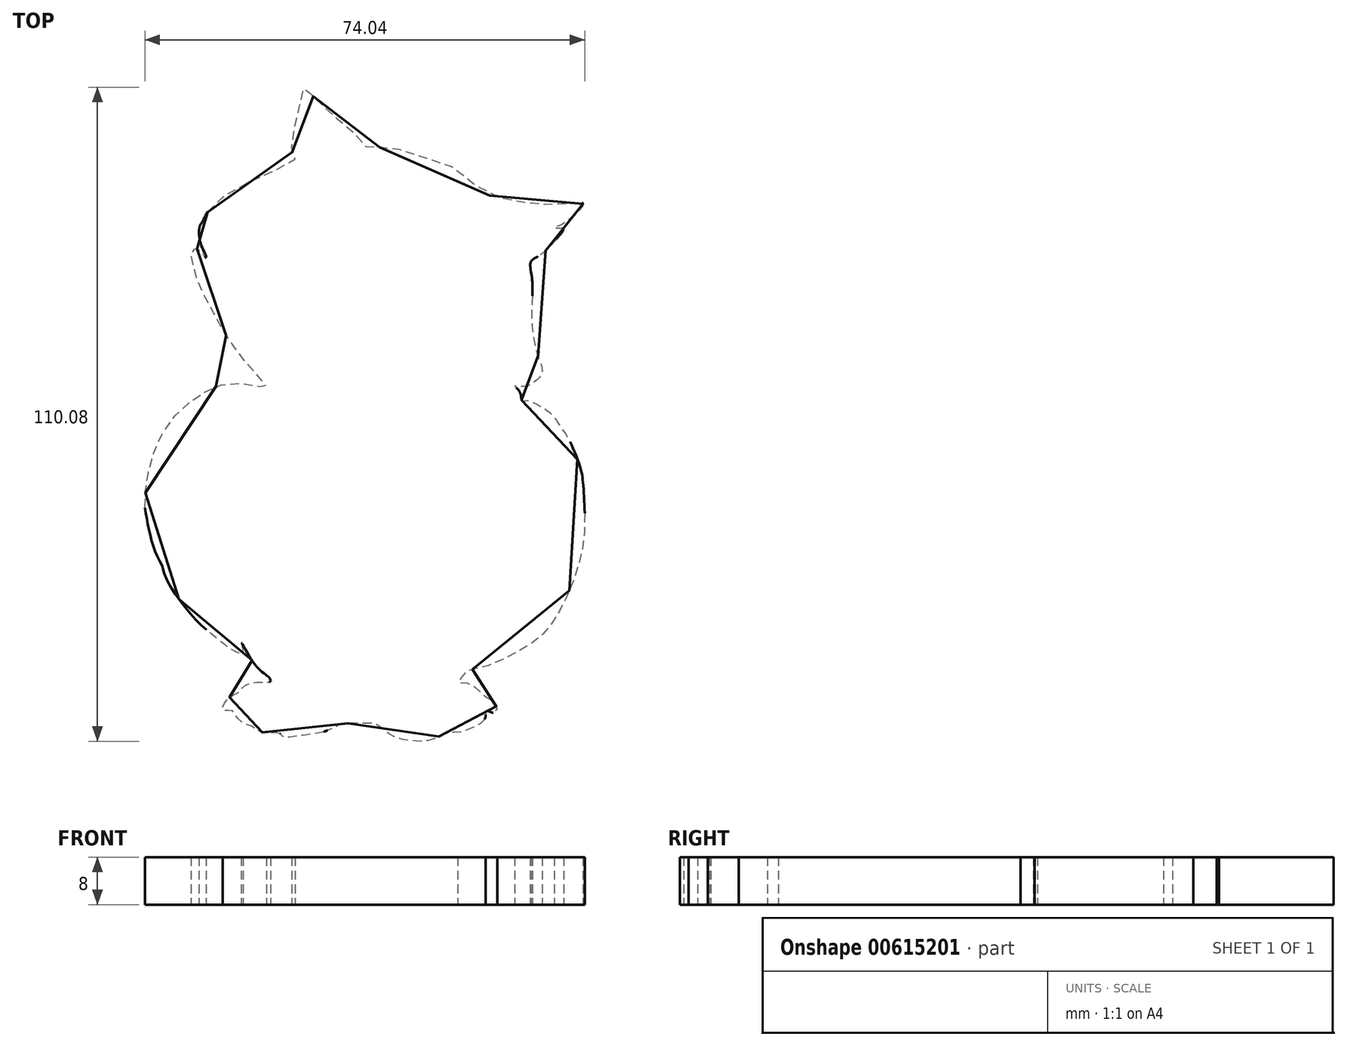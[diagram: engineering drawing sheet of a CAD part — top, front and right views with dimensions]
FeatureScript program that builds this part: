
annotation { "Feature Type Name" : "Feature", "Feature Type Description" : "" }
export const myFeature = defineFeature(function(context is Context, id is Id, definition is map)
    precondition{}
    {
        {
            var Q0;
            Q0=qCreatedBy(makeId("Top.planeOp"),FACE);
            var sketch = newSketch(context, id + "F0", { "sketchPlane" : qUnion([Q0])});
            skFitSpline(sketch, "E0", {"points": [v(-60.93, 34.26) * mm, v(-58.9, 36.4) * mm, v(-54.12, 39.26) * mm, v(-49.9, 41.11) * mm, v(-46.23, 43.1) * mm, v(-46.36, 43.53) * mm, v(-46.75, 44.5) * mm, v(-46.75, 45.72) * mm, v(-46.32, 48.48) * mm, v(-45.62, 51.45) * mm, v(-45.05, 53.74) * mm, v(-44.67, 55.24) * mm, v(-44.57, 55.2) * mm, v(-44.17, 54.78) * mm, v(-43.15, 53.73) * mm, v(-41.65, 52.25) * mm, v(-40.17, 50.8) * mm, v(-38.14, 49.23) * mm, v(-35.8, 47.02) * mm, v(-34.35, 45.32) * mm, v(-34.13, 45.26) * mm, v(-32.08, 45.14) * mm, v(-30.65, 45.1) * mm, v(-28.26, 44.71) * mm, v(-23.01, 42.96) * mm, v(-18.64, 41.21) * mm, v(-13.39, 37.01) * mm, v(-10.48, 36.6) * mm, v(-6.86, 35.71) * mm, v(-4.31, 35.58) * mm, v(-0.84, 35.67) * mm, v(1.02, 35.9) * mm, v(2.22, 35.71) * mm, v(1.76, 34.7) * mm, v(0, 33.07) * mm, v(-1.76, 31.96) * mm, v(-2.6, 31.64) * mm, v(-2.04, 31.59) * mm, v(-1.02, 31.5) * mm, v(-1.2, 30.99) * mm, v(-3.2, 28.62) * mm, v(-5.24, 26.86) * mm, v(-6.54, 25.84) * mm, v(-6.4, 23.52) * mm, v(-6.3, 19.68) * mm, v(-6.17, 13.56) * mm, v(-5, 9.1) * mm, v(-4.64, 7.81) * mm, v(-4.92, 6.56) * mm, v(-5.8, 5.79) * mm, v(-7.13, 4.98) * mm, v(-8.79, 4.98) * mm, v(-9.26, 4.98) * mm, v(-8.86, 4.58) * mm, v(-8.2, 3.4) * mm, v(-8.01, 2.4) * mm, v(-7.2, 2.52) * mm, v(-6.03, 2.11) * mm, v(-4.6, 1.41) * mm, v(-2.83, 0) * mm, v(-1.58, -1.83) * mm, v(0, -4.3) * mm, v(1.77, -8.74) * mm, v(2.21, -10.91) * mm, v(2.54, -17.41) * mm, v(1.95, -23.53) * mm, v(0, -29.3) * mm, v(-2.44, -34.15) * mm, v(-5.26, -37.5) * mm, v(-9.46, -40.12) * mm, v(-14.94, -42.47) * mm, v(-17.3, -42.93) * mm, v(-17.72, -43.53) * mm, v(-18.83, -44.83) * mm, v(-17.86, -44.92) * mm, v(-16.33, -45.48) * mm, v(-15.17, -46.27) * mm, v(-14.75, -47.01) * mm, v(-13.6, -47.52) * mm, v(-12.3, -49.1) * mm, v(-12.39, -50.12) * mm, v(-14.06, -49.7) * mm, v(-14.15, -50.2) * mm, v(-14.52, -51.46) * mm, v(-16.98, -52.8) * mm, v(-18.55, -53.31) * mm, v(-20.45, -53.4) * mm, v(-22.46, -54.26) * mm, v(-24.74, -54.82) * mm, v(-27.86, -54.56) * mm, v(-30.3, -53.64) * mm, v(-32.54, -51.98) * mm, v(-34.45, -51.84) * mm, v(-37.98, -51.84) * mm, v(-38.97, -52.17) * mm, v(-41.33, -53.2) * mm, v(-45.41, -53.9) * mm, v(-48.24, -54.04) * mm, v(-48.8, -53.45) * mm, v(-50.56, -53.5) * mm, v(-52.59, -52.98) * mm, v(-53.65, -52.2) * mm, v(-54.65, -51.95) * mm, v(-55.9, -50.92) * mm, v(-56.49, -50.03) * mm, v(-56.98, -49.59) * mm, v(-58.03, -49.75) * mm, v(-58.39, -49.26) * mm, v(-58.16, -48.5) * mm, v(-57.2, -47.4) * mm, v(-55.77, -46.6) * mm, v(-55.18, -45.88) * mm, v(-54.06, -45.2) * mm, v(-52.23, -44.87) * mm, v(-50.46, -44.87) * mm, v(-50.4, -44.38) * mm, v(-51.18, -43.62) * mm, v(-53.27, -41.5) * mm, v(-55.27, -38.28) * mm, v(-55.04, -39.92) * mm, v(-57.1, -39.23) * mm, v(-59.67, -37.3) * mm, v(-64.02, -33.17) * mm, v(-68, -27.2) * mm, v(-68.58, -25.4) * mm, v(-69.91, -22.49) * mm, v(-70.96, -18.46) * mm, v(-71.49, -14.96) * mm, v(-71.14, -10.76) * mm, v(-69.81, -5.7) * mm, v(-66.43, 0) * mm, v(-62.14, 3.5) * mm, v(-58.54, 5.16) * mm, v(-53.02, 5.1) * mm, v(-51.07, 4.73) * mm, v(-52.18, 6.36) * mm, v(-54.87, 9.42) * mm, v(-58.16, 14.05) * mm, v(-60.06, 17.53) * mm, v(-62.43, 22.12) * mm, v(-63.17, 24.62) * mm, v(-63.72, 26.75) * mm, v(-63.52, 27.92) * mm, v(-62.9, 28.1) * mm, v(-62.18, 27.9) * mm, v(-61.83, 27.16) * mm, v(-61.42, 26.58) * mm, v(-61.18, 26.72) * mm, v(-61.33, 27.22) * mm, v(-61.91, 28.39) * mm, v(-62.26, 29.7) * mm, v(-62.32, 31.66) * mm, v(-61.6, 33.03) * mm, v(-60.93, 34.26) * mm]});
            skSolve(sketch);
        }
        {
            var Q0;
            Q0 = qSketchRegion(id + "F0", true);
            extrude(context, id + "F1", {"entities" : qUnion([Q0]), "depth" : 8 * mm, "offsetDistance" : 25 * mm});
        }
    });
